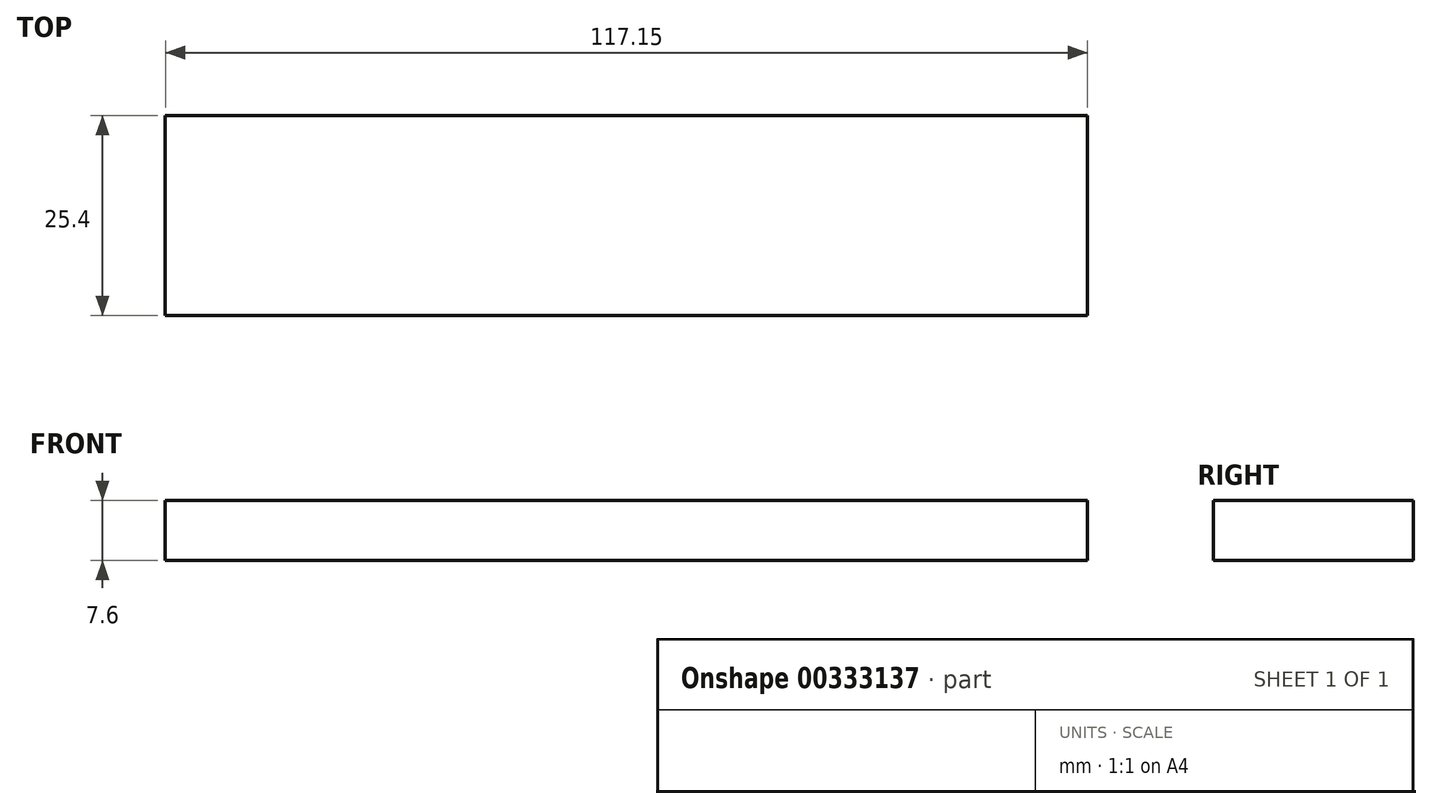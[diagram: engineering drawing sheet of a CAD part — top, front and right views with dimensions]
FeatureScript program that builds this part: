
annotation { "Feature Type Name" : "Feature", "Feature Type Description" : "" }
export const myFeature = defineFeature(function(context is Context, id is Id, definition is map)
    precondition{}
    {
        {
            var Q0;
            Q0=qCreatedBy(makeId("Front.planeOp"),FACE);
            var sketch = newSketch(context, id + "F0", { "sketchPlane" : qUnion([Q0])});
            skLineSegment(sketch, "E0.bottom", {"start": v(-55.23, 13.22) * mm, "end": v(61.92, 13.22) * mm});
            skLineSegment(sketch, "E0.top", {"start": v(-55.23, 20.82) * mm, "end": v(61.92, 20.82) * mm});
            skLineSegment(sketch, "E0.left", {"start": v(-55.23, 13.22) * mm, "end": v(-55.23, 20.82) * mm});
            skLineSegment(sketch, "E0.right", {"start": v(61.92, 13.22) * mm, "end": v(61.92, 20.82) * mm});
            skSolve(sketch);
        }
        {
            var Q0;
            Q0 = qSketchRegion(id + "F0", true);
            extrude(context, id + "F1", {"entities" : qUnion([Q0]), "depth" : 25.4 * mm});
        }
    });
